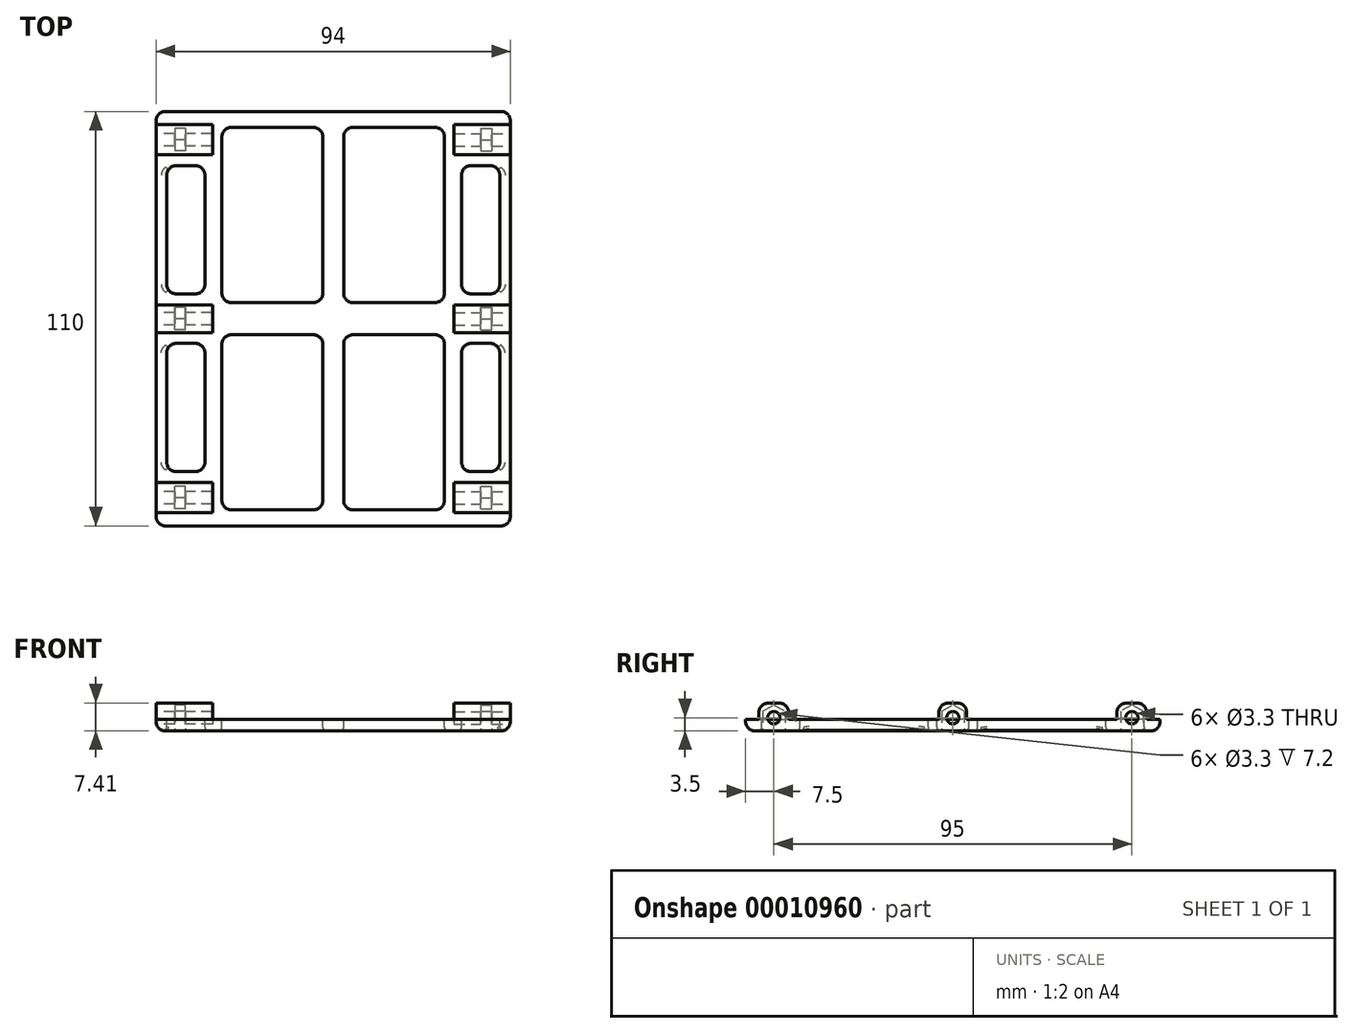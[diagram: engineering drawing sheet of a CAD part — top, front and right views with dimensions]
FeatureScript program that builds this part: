
annotation { "Feature Type Name" : "Feature", "Feature Type Description" : "" }
export const myFeature = defineFeature(function(context is Context, id is Id, definition is map)
    precondition{}
    {
        {
            var Q0;
            Q0=qCreatedBy(makeId("Right.planeOp"),FACE);
            var sketch = newSketch(context, id + "F0", { "sketchPlane" : qUnion([Q0])});
            skLineSegment(sketch, "E0.bottom", {"start": v(-55, 1.5) * mm, "end": v(0, 1.5) * mm});
            skLineSegment(sketch, "E0.top", {"start": v(-55, -1.5) * mm, "end": v(0, -1.5) * mm});
            skLineSegment(sketch, "E0.left", {"start": v(-55, 1.5) * mm, "end": v(-55, -1.5) * mm});
            skLineSegment(sketch, "E0.right", {"start": v(0, 1.5) * mm, "end": v(0, -1.5) * mm});
            skSolve(sketch);
        }
        {
            var Q0;
            Q0 = qSketchRegion(id + "F0", true);
            extrude(context, id + "F1", {"entities" : qUnion([Q0]), "depth" : (94 / 2) * mm});
        }
        {
            var Q0;
            Q0=makeQuery(id+"F1.opExtrude","CAP_FACE",FACE,{"disambiguationData":[OSD([sQuery(id+"F0.wireOp",EDGE,"E0.bottom"),sQuery(id+"F0.wireOp",EDGE,"E0.top"),sQuery(id+"F0.wireOp",EDGE,"E0.left"),sQuery(id+"F0.wireOp",EDGE,"E0.right")])],"isStart":false});
            var sketch = newSketch(context, id + "F2", { "sketchPlane" : qUnion([Q0])});
            skCircle(sketch, "E1", {"center": v(-47.5, 2) * mm, "radius": 1.55 * mm});
            skArc(sketch, "E2", {"start": v(0, 3.55) * mm, "mid": v(-1.55, 2) * mm, "end": v(0, 0.45) * mm});
            skLineSegment(sketch, "E3", {"start": v(-43.5, 2) * mm, "end": v(0, 2) * mm, "construction": true});
            skLineSegment(sketch, "E4.bottom", {"start": v(-48.8, 5.91) * mm, "end": v(-46.2, 5.91) * mm});
            skLineSegment(sketch, "E4.top", {"start": v(-51.5, 1.5) * mm, "end": v(-43.5, 1.5) * mm});
            skLineSegment(sketch, "E4.left", {"start": v(-51.5, 3.21) * mm, "end": v(-51.5, 1.5) * mm});
            skLineSegment(sketch, "E4.right", {"start": v(-43.5, 3.21) * mm, "end": v(-43.5, 1.5) * mm});
            skLineSegment(sketch, "E5", {"start": v(-47.5, 5.91) * mm, "end": v(-47.5, 2) * mm, "construction": true});
            skLineSegment(sketch, "E6.bottom", {"start": v(-1.18, 5.91) * mm, "end": v(0, 5.91) * mm});
            skLineSegment(sketch, "E6.top", {"start": v(-3.68, 1.5) * mm, "end": v(0, 1.5) * mm});
            skLineSegment(sketch, "E6.left", {"start": v(-3.68, 3.41) * mm, "end": v(-3.68, 1.5) * mm});
            skLineSegment(sketch, "E6.right", {"start": v(0, 5.91) * mm, "end": v(0, 3.55) * mm});
            skLineSegment(sketch, "E7.trimOffspring", {"start": v(0, 1.5) * mm, "end": v(0, 0.45) * mm});
            skLineSegment(sketch, "E8", {"start": v(-43.5, 2) * mm, "end": v(-47.5, 2) * mm, "construction": true});
            skPoint(sketch, "E9.visualSharp", {"position": v(-43.5, 5.91) * mm});
            skArc(sketch, "E9.filletArc", {"start": v(-43.5, 3.21) * mm, "mid": v(-44.28, 5.12) * mm, "end": v(-46.2, 5.91) * mm});
            skPoint(sketch, "E10.visualSharp", {"position": v(-51.5, 5.91) * mm});
            skArc(sketch, "E10.filletArc", {"start": v(-48.8, 5.91) * mm, "mid": v(-50.72, 5.12) * mm, "end": v(-51.5, 3.21) * mm});
            skPoint(sketch, "E11.visualSharp", {"position": v(-3.68, 5.91) * mm});
            skArc(sketch, "E11.filletArc", {"start": v(-1.18, 5.91) * mm, "mid": v(-2.95, 5.18) * mm, "end": v(-3.68, 3.41) * mm});
            skSolve(sketch);
        }
        {
            var Q0;
            Q0 = qSketchRegion(id + "F2", true);
            extrude(context, id + "F3", {"entities" : qUnion([Q0]), "operationType" : NewBodyOperationType.ADD, "oppositeDirection" : true, "depth" : 15 * mm});
        }
        {
            var Q0;
            Q0=makeQuery(id+"F3.boolean.opBoolean","MERGE",FACE,{"derivedFrom":[makeQuery(id+"F1.opExtrude","CAP_FACE",FACE,{"disambiguationData":[OSD([sQuery(id+"F0.wireOp",EDGE,"E0.bottom"),sQuery(id+"F0.wireOp",EDGE,"E0.top"),sQuery(id+"F0.wireOp",EDGE,"E0.left"),sQuery(id+"F0.wireOp",EDGE,"E0.right")])],"isStart":false}),makeQuery(id+"F3.opExtrude","CAP_FACE",FACE,{"disambiguationData":[OSD([sQuery(id+"F2.wireOp",EDGE,"E1"),sQuery(id+"F2.wireOp",EDGE,"E4.bottom"),sQuery(id+"F2.wireOp",EDGE,"E4.top"),sQuery(id+"F2.wireOp",EDGE,"E4.left"),sQuery(id+"F2.wireOp",EDGE,"E4.right"),sQuery(id+"F2.wireOp",EDGE,"E9.filletArc"),sQuery(id+"F2.wireOp",EDGE,"E10.filletArc")])],"isStart":true}),makeQuery(id+"F3.opExtrude","CAP_FACE",FACE,{"disambiguationData":[OSD([sQuery(id+"F2.wireOp",EDGE,"E2"),sQuery(id+"F2.wireOp",EDGE,"E6.bottom"),sQuery(id+"F2.wireOp",EDGE,"E6.top"),sQuery(id+"F2.wireOp",EDGE,"E6.left"),sQuery(id+"F2.wireOp",EDGE,"E6.right"),sQuery(id+"F2.wireOp",EDGE,"E11.filletArc")])],"isStart":true})]});
            var sketch = newSketch(context, id + "F4", { "sketchPlane" : qUnion([Q0])});
            skCircle(sketch, "E12", {"center": v(-47.5, 2) * mm, "radius": 1.55 * mm});
            skCircle(sketch, "E13", {"center": v(0, 2) * mm, "radius": 1.55 * mm});
            skSolve(sketch);
        }
        {
            var Q0;
            Q0 = qSketchRegion(id + "F4", true);
            var Q1;
            Q1=makeQuery(id+"F3.opExtrude","CAP_FACE",FACE,{"disambiguationData":[OSD([sQuery(id+"F2.wireOp",EDGE,"E1"),sQuery(id+"F2.wireOp",EDGE,"E4.bottom"),sQuery(id+"F2.wireOp",EDGE,"E4.top"),sQuery(id+"F2.wireOp",EDGE,"E4.left"),sQuery(id+"F2.wireOp",EDGE,"E4.right"),sQuery(id+"F2.wireOp",EDGE,"E9.filletArc"),sQuery(id+"F2.wireOp",EDGE,"E10.filletArc")])],"isStart":false});
            extrude(context, id + "F5", {"entities" : qUnion([Q0]), "operationType" : NewBodyOperationType.REMOVE, "endBound" : BoundingType.UP_TO_SURFACE, "oppositeDirection" : true, "endBoundEntityFace" : qUnion([Q1]), "depth" : 20 * mm});
        }
        {
            var Q0;
            Q0=makeQuery(id+"F3.boolean.opBoolean","MERGE",FACE,{"derivedFrom":[makeQuery(id+"F1.opExtrude","CAP_FACE",FACE,{"disambiguationData":[OSD([sQuery(id+"F0.wireOp",EDGE,"E0.bottom"),sQuery(id+"F0.wireOp",EDGE,"E0.top"),sQuery(id+"F0.wireOp",EDGE,"E0.left"),sQuery(id+"F0.wireOp",EDGE,"E0.right")])],"isStart":false}),makeQuery(id+"F3.opExtrude","CAP_FACE",FACE,{"disambiguationData":[OSD([sQuery(id+"F2.wireOp",EDGE,"E1"),sQuery(id+"F2.wireOp",EDGE,"E4.bottom"),sQuery(id+"F2.wireOp",EDGE,"E4.top"),sQuery(id+"F2.wireOp",EDGE,"E4.left"),sQuery(id+"F2.wireOp",EDGE,"E4.right"),sQuery(id+"F2.wireOp",EDGE,"E9.filletArc"),sQuery(id+"F2.wireOp",EDGE,"E10.filletArc")])],"isStart":true}),makeQuery(id+"F3.opExtrude","CAP_FACE",FACE,{"disambiguationData":[OSD([sQuery(id+"F2.wireOp",EDGE,"E2"),sQuery(id+"F2.wireOp",EDGE,"E6.bottom"),sQuery(id+"F2.wireOp",EDGE,"E6.top"),sQuery(id+"F2.wireOp",EDGE,"E6.left"),sQuery(id+"F2.wireOp",EDGE,"E6.right"),sQuery(id+"F2.wireOp",EDGE,"E11.filletArc")])],"isStart":true})]});
            cPlane(context, id + "F6", {"entities" : qUnion([Q0]), "cplaneType" : CPlaneType.OFFSET, "offset" : 5 * mm, "oppositeDirection" : true, "width" : 150 * mm, "height" : 150 * mm});
        }
        {
            var Q0;
            Q0=qCreatedBy(id+"F6.planeOp",FACE);
            var sketch = newSketch(context, id + "F7", { "sketchPlane" : qUnion([Q0])});
            skCircle(sketch, "E14.cCircle", {"center": v(-47.5, 2) * mm, "radius": 2.95 * mm, "construction": true});
            skLineSegment(sketch, "E14.0", {"start": v(-47.5, -1.4) * mm, "end": v(-50.45, 0.3) * mm});
            skLineSegment(sketch, "E14.1", {"start": v(-50.45, 0.3) * mm, "end": v(-50.45, 3.7) * mm});
            skLineSegment(sketch, "E14.2", {"start": v(-50.45, 3.7) * mm, "end": v(-47.5, 5.4) * mm});
            skLineSegment(sketch, "E14.3", {"start": v(-47.5, 5.4) * mm, "end": v(-44.55, 3.7) * mm});
            skLineSegment(sketch, "E14.4", {"start": v(-44.55, 3.7) * mm, "end": v(-44.55, 0.3) * mm});
            skLineSegment(sketch, "E14.5", {"start": v(-44.55, 0.3) * mm, "end": v(-47.5, -1.4) * mm});
            skPoint(sketch, "E14.0.midPoint", {"position": v(-48.98, -0.55) * mm});
            skCircle(sketch, "E15.cCircle", {"center": v(0, 2) * mm, "radius": 2.95 * mm, "construction": true});
            skLineSegment(sketch, "E15.0", {"start": v(2.95, 0.3) * mm, "end": v(0, -1.4) * mm});
            skLineSegment(sketch, "E15.1", {"start": v(0, -1.4) * mm, "end": v(-2.95, 0.3) * mm});
            skLineSegment(sketch, "E15.2", {"start": v(-2.95, 0.3) * mm, "end": v(-2.95, 3.7) * mm});
            skLineSegment(sketch, "E15.3", {"start": v(-2.95, 3.7) * mm, "end": v(0, 5.4) * mm});
            skLineSegment(sketch, "E15.4", {"start": v(0, 5.4) * mm, "end": v(2.95, 3.7) * mm});
            skLineSegment(sketch, "E15.5", {"start": v(2.95, 3.7) * mm, "end": v(2.95, 0.3) * mm});
            skPoint(sketch, "E15.0.midPoint", {"position": v(1.48, -0.55) * mm});
            skLineSegment(sketch, "E16.bottom", {"start": v(-50.45, 0.3) * mm, "end": v(-44.55, 0.3) * mm});
            skLineSegment(sketch, "E16.top", {"start": v(-50.45, -1.5) * mm, "end": v(-44.55, -1.5) * mm});
            skLineSegment(sketch, "E16.left", {"start": v(-50.45, 0.3) * mm, "end": v(-50.45, -1.5) * mm});
            skLineSegment(sketch, "E16.right", {"start": v(-44.55, 0.3) * mm, "end": v(-44.55, -1.5) * mm});
            skLineSegment(sketch, "E17.bottom", {"start": v(-2.95, 0.3) * mm, "end": v(2.95, 0.3) * mm});
            skLineSegment(sketch, "E17.top", {"start": v(-2.95, -1.5) * mm, "end": v(2.95, -1.5) * mm});
            skLineSegment(sketch, "E17.left", {"start": v(-2.95, 0.3) * mm, "end": v(-2.95, -1.5) * mm});
            skLineSegment(sketch, "E17.right", {"start": v(2.95, 0.3) * mm, "end": v(2.95, -1.5) * mm});
            skSolve(sketch);
        }
        {
            var Q0;
            Q0 = qSketchRegion(id + "F7", true);
            extrude(context, id + "F8", {"entities" : qUnion([Q0]), "operationType" : NewBodyOperationType.REMOVE, "oppositeDirection" : true, "depth" : 2.8 * mm});
        }
        {
            var Q0;
            Q0=makeQuery(id+"F1.opExtrude","SWEPT_FACE",FACE,{"disambiguationData":[OSD([sQuery(id+"F0.wireOp",EDGE,"E0.bottom")])]});
            var sketch = newSketch(context, id + "F9", { "sketchPlane" : qUnion([Q0])});
            skLineSegment(sketch, "E18.bottom", {"start": v(5.26, -50.74) * mm, "end": v(27.03, -50.74) * mm});
            skLineSegment(sketch, "E18.top", {"start": v(5.26, -4.26) * mm, "end": v(27.03, -4.26) * mm});
            skLineSegment(sketch, "E18.left", {"start": v(2.76, -48.24) * mm, "end": v(2.76, -6.76) * mm});
            skLineSegment(sketch, "E18.right", {"start": v(29.53, -48.24) * mm, "end": v(29.53, -6.76) * mm});
            skPoint(sketch, "E19.visualSharp", {"position": v(2.76, -50.74) * mm});
            skArc(sketch, "E19.filletArc", {"start": v(2.76, -48.24) * mm, "mid": v(3.5, -50) * mm, "end": v(5.26, -50.74) * mm});
            skPoint(sketch, "E20.visualSharp", {"position": v(29.53, -50.74) * mm});
            skArc(sketch, "E20.filletArc", {"start": v(27.03, -50.74) * mm, "mid": v(28.8, -50) * mm, "end": v(29.53, -48.24) * mm});
            skPoint(sketch, "E21.visualSharp", {"position": v(29.53, -4.26) * mm});
            skArc(sketch, "E21.filletArc", {"start": v(29.53, -6.76) * mm, "mid": v(28.8, -5) * mm, "end": v(27.03, -4.26) * mm});
            skPoint(sketch, "E22.visualSharp", {"position": v(2.76, -4.26) * mm});
            skArc(sketch, "E22.filletArc", {"start": v(5.26, -4.26) * mm, "mid": v(3.5, -5) * mm, "end": v(2.76, -6.76) * mm});
            skLineSegment(sketch, "E23.top", {"start": v(36.56, -6.56) * mm, "end": v(41.67, -6.56) * mm});
            skArc(sketch, "E24.filletArc", {"start": v(34.06, -38.1) * mm, "mid": v(34.8, -39.88) * mm, "end": v(36.56, -40.6) * mm});
            skLineSegment(sketch, "E23.bottom", {"start": v(36.56, -40.6) * mm, "end": v(41.67, -40.6) * mm});
            skArc(sketch, "E25.filletArc", {"start": v(41.67, -40.6) * mm, "mid": v(43.44, -39.88) * mm, "end": v(44.17, -38.1) * mm});
            skArc(sketch, "E26.filletArc", {"start": v(44.17, -9.06) * mm, "mid": v(43.44, -7.3) * mm, "end": v(41.67, -6.56) * mm});
            skPoint(sketch, "E24.visualSharp", {"position": v(34.06, -40.6) * mm});
            skLineSegment(sketch, "E23.left", {"start": v(34.06, -38.1) * mm, "end": v(34.06, -9.06) * mm});
            skPoint(sketch, "E25.visualSharp", {"position": v(44.17, -40.6) * mm});
            skPoint(sketch, "E26.visualSharp", {"position": v(44.17, -6.56) * mm});
            skLineSegment(sketch, "E23.right", {"start": v(44.17, -38.1) * mm, "end": v(44.17, -9.06) * mm});
            skPoint(sketch, "E27.visualSharp", {"position": v(34.06, -6.56) * mm});
            skArc(sketch, "E27.filletArc", {"start": v(36.56, -6.56) * mm, "mid": v(34.8, -7.3) * mm, "end": v(34.06, -9.06) * mm});
            skLineSegment(sketch, "E28", {"start": v(47, -23.59) * mm, "end": v(44.17, -23.59) * mm, "construction": true});
            skLineSegment(sketch, "E29", {"start": v(2.76, -27.5) * mm, "end": v(0, -27.5) * mm, "construction": true});
            skSolve(sketch);
        }
        {
            var Q0;
            Q0 = qSketchRegion(id + "F9", true);
            extrude(context, id + "F10", {"entities" : qUnion([Q0]), "operationType" : NewBodyOperationType.REMOVE, "oppositeDirection" : true, "depth" : 25 * mm});
        }
        {
            var Q0;
            Q0=makeQuery(id+"F1.opExtrude","SWEPT_EDGE",EDGE,{"disambiguationData":[OSD([sQuery(id+"F0.wireOp",EDGE,"E0.top"),sQuery(id+"F0.wireOp",EDGE,"E0.left")])]});
            var Q1;
            Q1=makeQuery(id+"F1.opExtrude","CAP_EDGE",EDGE,{"disambiguationData":[OSD([sQuery(id+"F0.wireOp",EDGE,"E0.left")])],"isStart":false});
            var Q2;
            Q2=makeQuery(id+"F1.opExtrude","CAP_EDGE",EDGE,{"disambiguationData":[OSD([sQuery(id+"F0.wireOp",EDGE,"E0.top")])],"isStart":false});
            fillet(context, id + "F11", {"entities" : qUnion([Q0, Q1, Q2]), "radius" : 2.5 * mm, "tangentPropagation" : true, "allowEdgeOverflow" : false});
        }
        {
            var Q0;
            Q0=makeQuery(id+"F10.boolean.opBoolean","COPY",EDGE,{"derivedFrom":makeQuery(id+"F10.opExtrude","CAP_EDGE",EDGE,{"disambiguationData":[OSD([sQuery(id+"F9.wireOp",EDGE,"E18.left")])],"isStart":true})});
            var Q1;
            Q1=makeQuery(id+"F10.boolean.opBoolean","COPY",EDGE,{"derivedFrom":makeQuery(id+"F10.opExtrude","CAP_EDGE",EDGE,{"disambiguationData":[OSD([sQuery(id+"F9.wireOp",EDGE,"E23.left")])],"isStart":true})});
            var Q2;
            Q2=makeQuery(id+"F10.boolean.opBoolean","INTERSECT",EDGE,{"derivedFrom":[makeQuery(id+"F1.opExtrude","SWEPT_FACE",FACE,{"disambiguationData":[OSD([sQuery(id+"F0.wireOp",EDGE,"E0.top")])]}),makeQuery(id+"F10.opExtrude","SWEPT_FACE",FACE,{"disambiguationData":[OSD([sQuery(id+"F9.wireOp",EDGE,"E18.right")])]})]});
            var Q3;
            Q3=makeQuery(id+"F10.boolean.opBoolean","INTERSECT",EDGE,{"derivedFrom":[makeQuery(id+"F1.opExtrude","SWEPT_FACE",FACE,{"disambiguationData":[OSD([sQuery(id+"F0.wireOp",EDGE,"E0.top")])]}),makeQuery(id+"F10.opExtrude","SWEPT_FACE",FACE,{"disambiguationData":[OSD([sQuery(id+"F9.wireOp",EDGE,"E23.bottom")])]})]});
            fillet(context, id + "F12", {"entities" : qUnion([Q0, Q1, Q2, Q3]), "radius" : 1 * mm, "tangentPropagation" : true, "allowEdgeOverflow" : false});
        }
        {
            var Q0;
            Q0=makeQuery(id+"F3.boolean.opBoolean","MERGE",FACE,{"derivedFrom":[makeQuery(id+"F1.opExtrude","CAP_FACE",FACE,{"disambiguationData":[OSD([sQuery(id+"F0.wireOp",EDGE,"E0.bottom"),sQuery(id+"F0.wireOp",EDGE,"E0.top"),sQuery(id+"F0.wireOp",EDGE,"E0.left"),sQuery(id+"F0.wireOp",EDGE,"E0.right")])],"isStart":false}),makeQuery(id+"F3.opExtrude","CAP_FACE",FACE,{"disambiguationData":[OSD([sQuery(id+"F2.wireOp",EDGE,"E1"),sQuery(id+"F2.wireOp",EDGE,"E4.bottom"),sQuery(id+"F2.wireOp",EDGE,"E4.top"),sQuery(id+"F2.wireOp",EDGE,"E4.left"),sQuery(id+"F2.wireOp",EDGE,"E4.right"),sQuery(id+"F2.wireOp",EDGE,"E9.filletArc"),sQuery(id+"F2.wireOp",EDGE,"E10.filletArc")])],"isStart":true}),makeQuery(id+"F3.opExtrude","CAP_FACE",FACE,{"disambiguationData":[OSD([sQuery(id+"F2.wireOp",EDGE,"E2"),sQuery(id+"F2.wireOp",EDGE,"E6.bottom"),sQuery(id+"F2.wireOp",EDGE,"E6.top"),sQuery(id+"F2.wireOp",EDGE,"E6.left"),sQuery(id+"F2.wireOp",EDGE,"E6.right"),sQuery(id+"F2.wireOp",EDGE,"E11.filletArc")])],"isStart":true})]});
            var sketch = newSketch(context, id + "F13", { "sketchPlane" : qUnion([Q0])});
            skCircle(sketch, "E30", {"center": v(-47.5, 2) * mm, "radius": 1.65 * mm});
            skCircle(sketch, "E31", {"center": v(0, 2) * mm, "radius": 1.65 * mm});
            skSolve(sketch);
        }
        {
            var Q0;
            Q0 = qSketchRegion(id + "F13", true);
            var Q1;
            Q1=makeQuery(id+"F3.opExtrude","CAP_FACE",FACE,{"disambiguationData":[OSD([sQuery(id+"F2.wireOp",EDGE,"E1"),sQuery(id+"F2.wireOp",EDGE,"E4.bottom"),sQuery(id+"F2.wireOp",EDGE,"E4.top"),sQuery(id+"F2.wireOp",EDGE,"E4.left"),sQuery(id+"F2.wireOp",EDGE,"E4.right"),sQuery(id+"F2.wireOp",EDGE,"E9.filletArc"),sQuery(id+"F2.wireOp",EDGE,"E10.filletArc")])],"isStart":false});
            extrude(context, id + "F14", {"entities" : qUnion([Q0]), "operationType" : NewBodyOperationType.REMOVE, "endBound" : BoundingType.UP_TO_SURFACE, "oppositeDirection" : true, "endBoundEntityFace" : qUnion([Q1]), "depth" : 25 * mm});
        }
        {
            var Q0;
            Q0=makeQuery(id+"F1.opExtrude","SWEPT_BODY",BODY,{"disambiguationData":[OSD([sQuery(id+"F0.wireOp",EDGE,"E0.bottom"),sQuery(id+"F0.wireOp",EDGE,"E0.top"),sQuery(id+"F0.wireOp",EDGE,"E0.left"),sQuery(id+"F0.wireOp",EDGE,"E0.right")])]});
            var Q1;
            {var subQ0=sQuery(id+"F0.wireOp",EDGE,"E0.right");var subQ4=sQuery(id+"F0.wireOp",EDGE,"E0.bottom");Q1=makeQuery(id+"F8.boolean.opBoolean","SPLIT",FACE,{"disambiguationData":[TD([makeQuery(id+"F1.opExtrude","SWEPT_FACE",FACE,{"disambiguationData":[OSD([subQ4])]})])],"derivedFrom":makeQuery(id+"F1.opExtrude","SWEPT_FACE",FACE,{"disambiguationData":[OSD([subQ0])]})});}
            mirror(context, id + "F15", {"operationType" : NewBodyOperationType.ADD, "entities" : qUnion([Q0]), "mirrorPlane" : qUnion([Q1])});
        }
        {
            var Q0;
            Q0=makeQuery(id+"F1.opExtrude","SWEPT_BODY",BODY,{"disambiguationData":[OSD([sQuery(id+"F0.wireOp",EDGE,"E0.bottom"),sQuery(id+"F0.wireOp",EDGE,"E0.top"),sQuery(id+"F0.wireOp",EDGE,"E0.left"),sQuery(id+"F0.wireOp",EDGE,"E0.right")])]});
            var Q1;
            {var subQ0=makeQuery(id+"F1.opExtrude","CAP_FACE",FACE,{"disambiguationData":[OSD([sQuery(id+"F0.wireOp",EDGE,"E0.bottom"),sQuery(id+"F0.wireOp",EDGE,"E0.top"),sQuery(id+"F0.wireOp",EDGE,"E0.left"),sQuery(id+"F0.wireOp",EDGE,"E0.right")])],"isStart":true});Q1=makeQuery(id+"F15.boolean.opBoolean","MERGE",FACE,{"derivedFrom":[subQ0,makeQuery(id+"F15.opPattern","COPY",FACE,{"derivedFrom":subQ0,"instanceName":"1"})]});}
            mirror(context, id + "F16", {"operationType" : NewBodyOperationType.ADD, "entities" : qUnion([Q0]), "mirrorPlane" : qUnion([Q1])});
        }
    });
